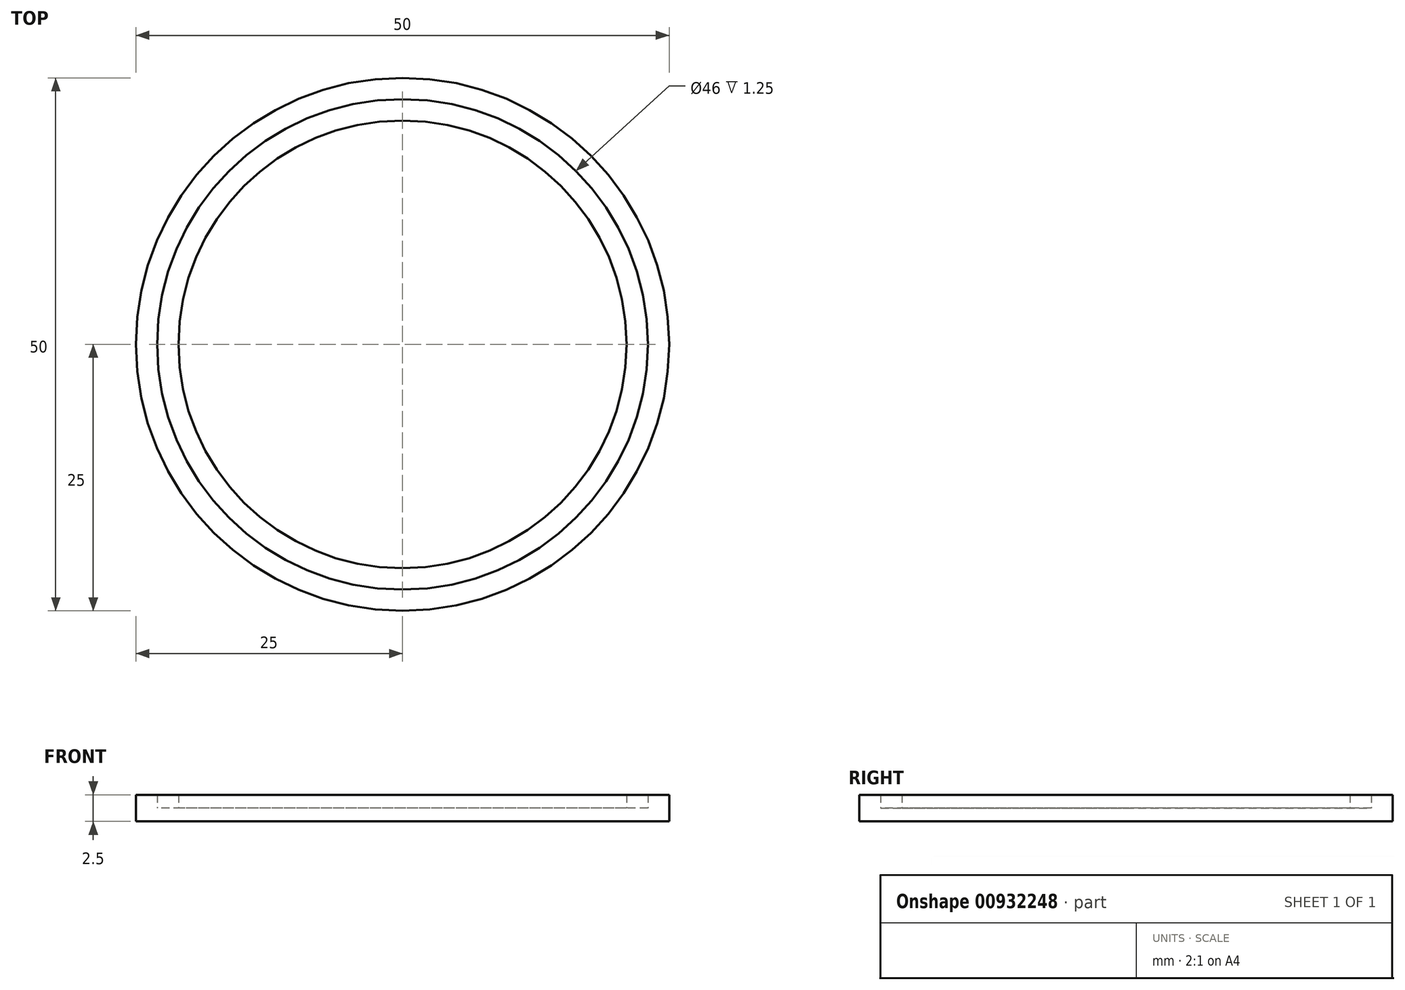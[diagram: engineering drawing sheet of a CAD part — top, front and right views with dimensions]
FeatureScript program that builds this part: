
annotation { "Feature Type Name" : "Feature", "Feature Type Description" : "" }
export const myFeature = defineFeature(function(context is Context, id is Id, definition is map)
    precondition{}
    {
        {
            var Q0;
            Q0=qCreatedBy(makeId("Top.planeOp"),FACE);
            var sketch = newSketch(context, id + "F0", { "sketchPlane" : qUnion([Q0])});
            skCircle(sketch, "E0", {"center": v(0, 0) * mm, "radius": 25 * mm});
            skCircle(sketch, "E1", {"center": v(0, 0) * mm, "radius": 23 * mm});
            skCircle(sketch, "E2.0", {"center": v(0, 0) * mm, "radius": 21 * mm});
            skSolve(sketch);
        }
        {
            var Q0;
            Q0=makeQuery(id+"F0.imprint","IMPRINT",FACE,{"disambiguationData":[TD([[makeQuery(id+"F0.imprint","IMPRINT",EDGE,{"derivedFrom":sQuery(id+"F0.wireOp",EDGE,"E0")}),1.0]])]});
            var Q1;
            Q1=makeQuery(id+"F0.imprint","IMPRINT",FACE,{"disambiguationData":[TD([[makeQuery(id+"F0.imprint","IMPRINT",EDGE,{"derivedFrom":sQuery(id+"F0.wireOp",EDGE,"E2.0")}),1.0]])]});
            var Q2;
            Q2=makeQuery(id+"F0.imprint","IMPRINT",FACE,{"disambiguationData":[TD([[makeQuery(id+"F0.imprint","IMPRINT",EDGE,{"derivedFrom":sQuery(id+"F0.wireOp",EDGE,"E1")}),1.0]])]});
            extrude(context, id + "F1", {"entities" : qUnion([Q0, Q1, Q2]), "endBound" : BoundingType.SYMMETRIC, "depth" : 2.5 * mm, "offsetDistance" : 25 * mm});
        }
        {
            var Q0;
            Q0=makeQuery(id+"F0.imprint","IMPRINT",FACE,{"disambiguationData":[TD([[makeQuery(id+"F0.imprint","IMPRINT",EDGE,{"derivedFrom":sQuery(id+"F0.wireOp",EDGE,"E1")}),1.0]])]});
            extrude(context, id + "F2", {"entities" : qUnion([Q0]), "operationType" : NewBodyOperationType.REMOVE, "depth" : 25 * mm, "offsetDistance" : 25 * mm});
        }
    });
